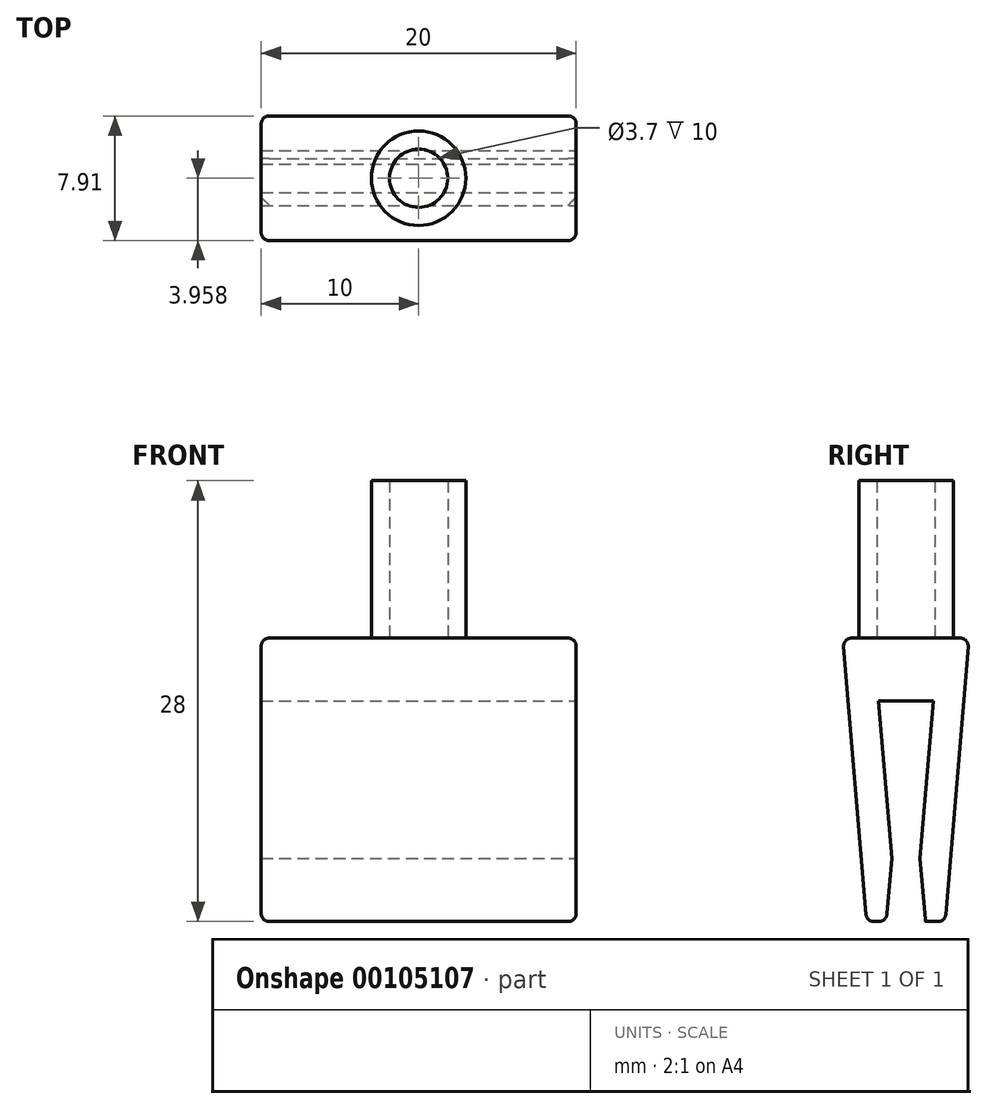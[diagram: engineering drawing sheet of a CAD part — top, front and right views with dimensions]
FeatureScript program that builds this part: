
annotation { "Feature Type Name" : "Feature", "Feature Type Description" : "" }
export const myFeature = defineFeature(function(context is Context, id is Id, definition is map)
    precondition{}
    {
        {
            var Q0;
            Q0=qCreatedBy(makeId("Right.planeOp"),FACE);
            var sketch = newSketch(context, id + "F0", { "sketchPlane" : qUnion([Q0])});
            skLineSegment(sketch, "E0", {"start": v(-44.08, 9.29) * mm, "end": v(-45.58, 27.29) * mm});
            skLineSegment(sketch, "E1", {"start": v(-45.58, 27.29) * mm, "end": v(-37.58, 27.29) * mm});
            skLineSegment(sketch, "E2", {"start": v(-37.58, 27.29) * mm, "end": v(-39.08, 9.29) * mm});
            skLineSegment(sketch, "E3", {"start": v(-39.08, 9.29) * mm, "end": v(-44.08, 9.29) * mm});
            skSolve(sketch);
        }
        {
            var Q0;
            Q0 = qSketchRegion(id + "F0", true);
            extrude(context, id + "F1", {"entities" : qUnion([Q0]), "endBound" : BoundingType.SYMMETRIC, "depth" : 20 * mm});
        }
        {
            var Q0;
            Q0=makeQuery(id+"F1.opExtrude","CAP_FACE",FACE,{"disambiguationData":[OSD([sQuery(id+"F0.wireOp",EDGE,"E0"),sQuery(id+"F0.wireOp",EDGE,"E1"),sQuery(id+"F0.wireOp",EDGE,"E2"),sQuery(id+"F0.wireOp",EDGE,"E3")])],"isStart":false});
            var sketch = newSketch(context, id + "F2", { "sketchPlane" : qUnion([Q0])});
            skLineSegment(sketch, "E4", {"start": v(-40.33, 9.29) * mm, "end": v(-40.68, 13.29) * mm});
            skLineSegment(sketch, "E5", {"start": v(-40.68, 13.29) * mm, "end": v(-39.83, 23.29) * mm});
            skLineSegment(sketch, "E6", {"start": v(-39.83, 23.29) * mm, "end": v(-41.58, 23.29) * mm});
            skLineSegment(sketch, "E7.MirrorCS", {"start": v(-43.33, 23.29) * mm, "end": v(-41.58, 23.29) * mm});
            skLineSegment(sketch, "E8.MirrorCS", {"start": v(-42.48, 13.29) * mm, "end": v(-43.33, 23.29) * mm});
            skLineSegment(sketch, "E9.MirrorCS", {"start": v(-42.83, 9.29) * mm, "end": v(-42.48, 13.29) * mm});
            skSolve(sketch);
        }
        {
            var Q0;
            {var subQ0=sQuery(id+"F2.wireOp",EDGE,"E4");Q0=makeQuery(id+"F2.imprint","IMPRINT",FACE,{"disambiguationData":[TD([[makeQuery(id+"F2.imprint","IMPRINT",EDGE,{"derivedFrom":subQ0}),1.0]])]});}
            extrude(context, id + "F3", {"entities" : qUnion([Q0]), "operationType" : NewBodyOperationType.REMOVE, "oppositeDirection" : true, "depth" : 25 * mm});
        }
        {
            var Q0;
            Q0=makeQuery(id+"F1.opExtrude","CAP_EDGE",EDGE,{"disambiguationData":[OSD([sQuery(id+"F0.wireOp",EDGE,"E0")])],"isStart":false});
            var Q1;
            Q1=makeQuery(id+"F1.opExtrude","CAP_EDGE",EDGE,{"disambiguationData":[OSD([sQuery(id+"F0.wireOp",EDGE,"E1")])],"isStart":false});
            var Q2;
            Q2=makeQuery(id+"F1.opExtrude","CAP_EDGE",EDGE,{"disambiguationData":[OSD([sQuery(id+"F0.wireOp",EDGE,"E2")])],"isStart":false});
            var Q3;
            Q3=makeQuery(id+"F1.opExtrude","SWEPT_EDGE",EDGE,{"disambiguationData":[OSD([sQuery(id+"F0.wireOp",EDGE,"E2"),sQuery(id+"F0.wireOp",EDGE,"E3")])]});
            var Q4;
            Q4=makeQuery(id+"F1.opExtrude","SWEPT_EDGE",EDGE,{"disambiguationData":[OSD([sQuery(id+"F0.wireOp",EDGE,"E0"),sQuery(id+"F0.wireOp",EDGE,"E3")])]});
            var Q5;
            Q5=makeQuery(id+"F1.opExtrude","CAP_EDGE",EDGE,{"disambiguationData":[OSD([sQuery(id+"F0.wireOp",EDGE,"E0")])],"isStart":true});
            var Q6;
            Q6=makeQuery(id+"F1.opExtrude","CAP_EDGE",EDGE,{"disambiguationData":[OSD([sQuery(id+"F0.wireOp",EDGE,"E2")])],"isStart":true});
            var Q7;
            Q7=makeQuery(id+"F1.opExtrude","SWEPT_EDGE",EDGE,{"disambiguationData":[OSD([sQuery(id+"F0.wireOp",EDGE,"E1"),sQuery(id+"F0.wireOp",EDGE,"E2")])]});
            var Q8;
            Q8=makeQuery(id+"F1.opExtrude","SWEPT_EDGE",EDGE,{"disambiguationData":[OSD([sQuery(id+"F0.wireOp",EDGE,"E0"),sQuery(id+"F0.wireOp",EDGE,"E1")])]});
            var Q9;
            Q9=makeQuery(id+"F1.opExtrude","CAP_EDGE",EDGE,{"disambiguationData":[OSD([sQuery(id+"F0.wireOp",EDGE,"E1")])],"isStart":true});
            var Q10;
            {var subQ0=sQuery(id+"F0.wireOp",EDGE,"E3");var subQ1=sQuery(id+"F0.wireOp",EDGE,"E2");Q10=makeQuery(id+"F3.boolean.opBoolean","SPLIT",EDGE,{"disambiguationData":[TD([makeQuery(id+"F1.opExtrude","SWEPT_FACE",FACE,{"disambiguationData":[OSD([subQ1])]})])],"derivedFrom":makeQuery(id+"F1.opExtrude","CAP_EDGE",EDGE,{"disambiguationData":[OSD([subQ0])],"isStart":true})});}
            var Q11;
            Q11=makeQuery(id+"F3.boolean.opBoolean","COPY",EDGE,{"derivedFrom":makeQuery(id+"F3.opExtrude","SWEPT_EDGE",EDGE,{"disambiguationData":[OSD([sQuery(id+"F0.wireOp",EDGE,"E3"),sQuery(id+"F2.wireOp",EDGE,"E4")])]})});
            var Q12;
            {var subQ0=sQuery(id+"F0.wireOp",EDGE,"E0");var subQ1=sQuery(id+"F0.wireOp",EDGE,"E3");Q12=makeQuery(id+"F3.boolean.opBoolean","SPLIT",EDGE,{"disambiguationData":[TD([makeQuery(id+"F1.opExtrude","SWEPT_FACE",FACE,{"disambiguationData":[OSD([subQ0])]})])],"derivedFrom":makeQuery(id+"F1.opExtrude","CAP_EDGE",EDGE,{"disambiguationData":[OSD([subQ1])],"isStart":true})});}
            var Q13;
            Q13=makeQuery(id+"F3.boolean.opBoolean","COPY",EDGE,{"derivedFrom":makeQuery(id+"F3.opExtrude","SWEPT_EDGE",EDGE,{"disambiguationData":[OSD([sQuery(id+"F0.wireOp",EDGE,"E3"),sQuery(id+"F2.wireOp",EDGE,"E9.MirrorCS")])]})});
            var Q14;
            {var subQ0=sQuery(id+"F0.wireOp",EDGE,"E3");var subQ1=sQuery(id+"F0.wireOp",EDGE,"E2");Q14=makeQuery(id+"F3.boolean.opBoolean","SPLIT",EDGE,{"disambiguationData":[TD([makeQuery(id+"F1.opExtrude","SWEPT_FACE",FACE,{"disambiguationData":[OSD([subQ1])]})])],"derivedFrom":makeQuery(id+"F1.opExtrude","CAP_EDGE",EDGE,{"disambiguationData":[OSD([subQ0])],"isStart":false})});}
            var Q15;
            {var subQ0=sQuery(id+"F0.wireOp",EDGE,"E0");var subQ1=sQuery(id+"F0.wireOp",EDGE,"E3");Q15=makeQuery(id+"F3.boolean.opBoolean","SPLIT",EDGE,{"disambiguationData":[TD([makeQuery(id+"F1.opExtrude","SWEPT_FACE",FACE,{"disambiguationData":[OSD([subQ0])]})])],"derivedFrom":makeQuery(id+"F1.opExtrude","CAP_EDGE",EDGE,{"disambiguationData":[OSD([subQ1])],"isStart":false})});}
            fillet(context, id + "F4", {"entities" : qUnion([Q0, Q1, Q2, Q3, Q4, Q5, Q6, Q7, Q8, Q9, Q10, Q11, Q12, Q13, Q14, Q15]), "radius" : 0.5 * mm, "tangentPropagation" : true, "allowEdgeOverflow" : false});
        }
        {
            var Q0;
            Q0=makeQuery(id+"F1.opExtrude","SWEPT_FACE",FACE,{"disambiguationData":[OSD([sQuery(id+"F0.wireOp",EDGE,"E1")])]});
            var sketch = newSketch(context, id + "F5", { "sketchPlane" : qUnion([Q0])});
            skCircle(sketch, "E10", {"center": v(0, -41.58) * mm, "radius": 1.85 * mm});
            skPoint(sketch, "E10.centerSnap0", {"position": v(-9.5, -41.58) * mm});
            skCircle(sketch, "E11", {"center": v(0, -41.58) * mm, "radius": 3 * mm});
            skSolve(sketch);
        }
        {
            var Q0;
            Q0=makeQuery(id+"F5.imprint","IMPRINT",FACE,{"disambiguationData":[TD([[makeQuery(id+"F5.imprint","IMPRINT",EDGE,{"derivedFrom":sQuery(id+"F5.wireOp",EDGE,"E10")}),-1.0]])]});
            extrude(context, id + "F6", {"entities" : qUnion([Q0]), "operationType" : NewBodyOperationType.ADD, "depth" : 10 * mm});
        }
    });
